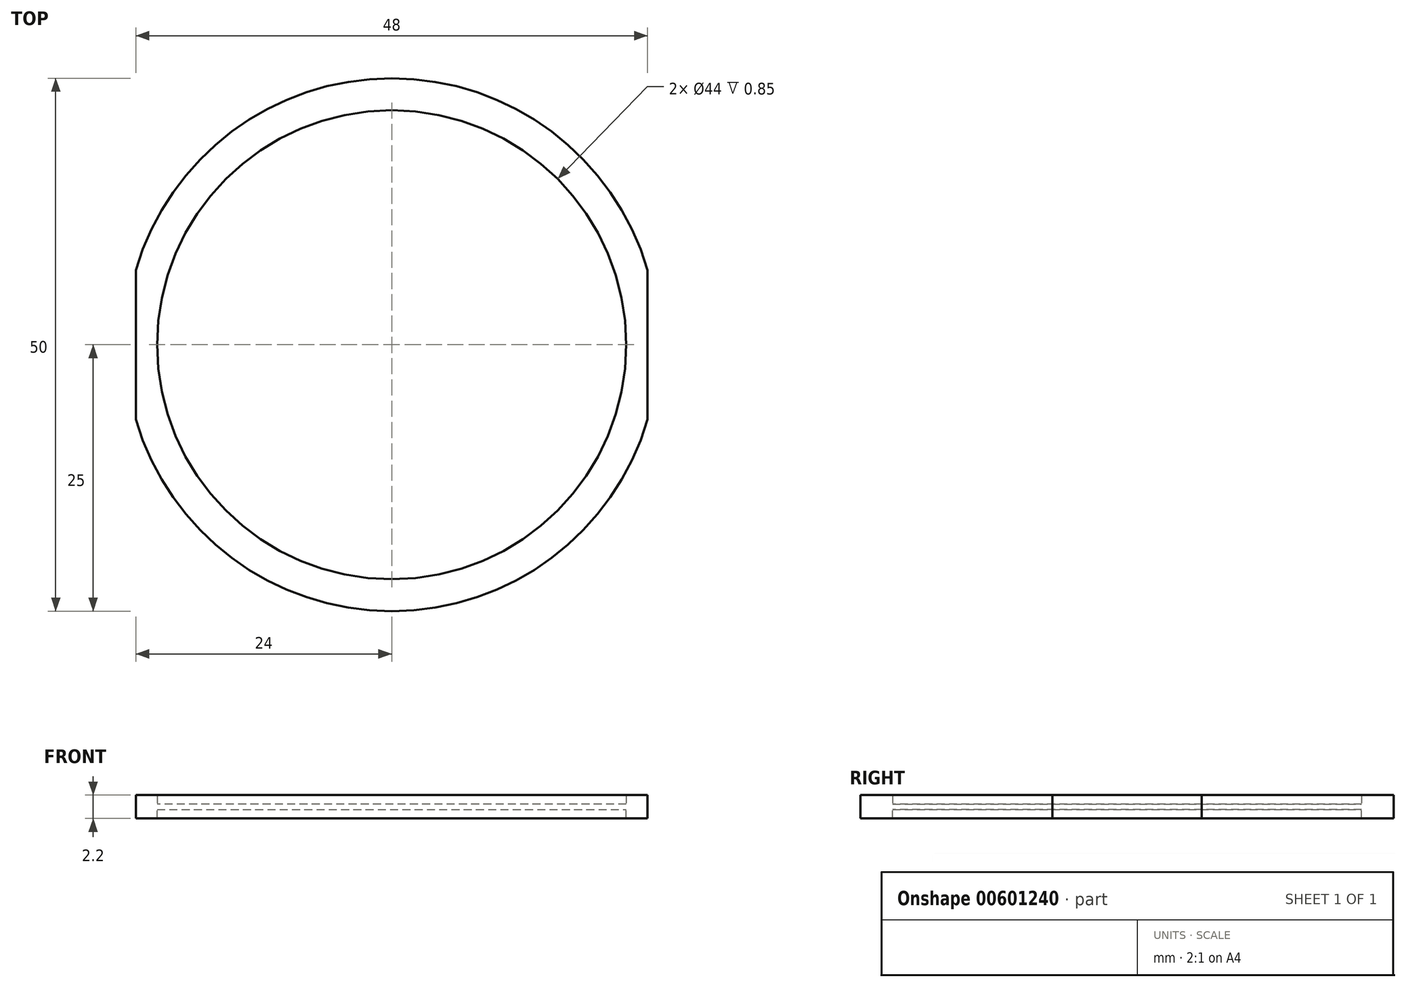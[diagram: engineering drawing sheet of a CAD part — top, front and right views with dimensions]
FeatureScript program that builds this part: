
annotation { "Feature Type Name" : "Feature", "Feature Type Description" : "" }
export const myFeature = defineFeature(function(context is Context, id is Id, definition is map)
    precondition{}
    {
        {
            var Q0;
            Q0=qCreatedBy(makeId("Top.planeOp"),FACE);
            var sketch = newSketch(context, id + "F0", { "sketchPlane" : qUnion([Q0])});
            skArc(sketch, "E0", {"start": v(24, 7) * mm, "mid": v(0, 25) * mm, "end": v(-24, 7) * mm});
            skLineSegment(sketch, "E1.left", {"start": v(-24, 7) * mm, "end": v(-24, -7) * mm});
            skLineSegment(sketch, "E1.right", {"start": v(24, 7) * mm, "end": v(24, -7) * mm});
            skArc(sketch, "E2.trimOffspring", {"start": v(-24, -7) * mm, "mid": v(0, -25) * mm, "end": v(24, -7) * mm});
            skSolve(sketch);
        }
        {
            var Q0;
            Q0=makeQuery(id+"F0.imprint","IMPRINT",FACE,{"disambiguationData":[TD([[makeQuery(id+"F0.imprint","IMPRINT",EDGE,{"derivedFrom":sQuery(id+"F0.wireOp",EDGE,"E0")}),1.0]])]});
            extrude(context, id + "F1", {"entities" : qUnion([Q0]), "depth" : 0.5 * mm, "offsetDistance" : 25 * mm});
        }
        {
            var Q0;
            Q0=makeQuery(id+"F1.opExtrude","CAP_FACE",FACE,{"disambiguationData":[OSD([sQuery(id+"F0.wireOp",EDGE,"E0"),sQuery(id+"F0.wireOp",EDGE,"E1.left"),sQuery(id+"F0.wireOp",EDGE,"E1.right"),sQuery(id+"F0.wireOp",EDGE,"E2.trimOffspring")])],"isStart":false});
            var sketch = newSketch(context, id + "F2", { "sketchPlane" : qUnion([Q0])});
            skCircle(sketch, "E3", {"center": v(0, 0) * mm, "radius": 22 * mm});
            skArc(sketch, "E4", {"start": v(24, -7) * mm, "mid": v(0, -25) * mm, "end": v(-24, -7) * mm});
            skArc(sketch, "E5", {"start": v(-24, 7) * mm, "mid": v(0, 25) * mm, "end": v(24, 7) * mm});
            skLineSegment(sketch, "E6", {"start": v(24, 7) * mm, "end": v(24, -7) * mm});
            skLineSegment(sketch, "E7", {"start": v(-24, 7) * mm, "end": v(-24, -7) * mm});
            skSolve(sketch);
        }
        {
            var Q0;
            Q0=makeQuery(id+"F2.imprint","IMPRINT",FACE,{"disambiguationData":[TD([[makeQuery(id+"F2.imprint","IMPRINT",EDGE,{"derivedFrom":sQuery(id+"F2.wireOp",EDGE,"E3")}),-1.0]])]});
            extrude(context, id + "F3", {"entities" : qUnion([Q0]), "operationType" : NewBodyOperationType.ADD, "depth" : 0.85 * mm, "offsetDistance" : 25 * mm});
        }
        {
            var Q0;
            Q0=makeQuery(id+"F1.opExtrude","CAP_FACE",FACE,{"disambiguationData":[OSD([sQuery(id+"F0.wireOp",EDGE,"E0"),sQuery(id+"F0.wireOp",EDGE,"E1.left"),sQuery(id+"F0.wireOp",EDGE,"E1.right"),sQuery(id+"F0.wireOp",EDGE,"E2.trimOffspring")])],"isStart":true});
            var sketch = newSketch(context, id + "F4", { "sketchPlane" : qUnion([Q0])});
            skCircle(sketch, "E8", {"center": v(0, 0) * mm, "radius": 22 * mm});
            skArc(sketch, "E9", {"start": v(-24, 7) * mm, "mid": v(0, 25) * mm, "end": v(24, 7) * mm});
            skArc(sketch, "E10", {"start": v(24, -7) * mm, "mid": v(0, -25) * mm, "end": v(-24, -7) * mm});
            skLineSegment(sketch, "E11", {"start": v(24, 7) * mm, "end": v(24, -7) * mm});
            skLineSegment(sketch, "E12", {"start": v(-24, 7) * mm, "end": v(-24, -7) * mm});
            skSolve(sketch);
        }
        {
            var Q0;
            Q0=makeQuery(id+"F4.imprint","IMPRINT",FACE,{"disambiguationData":[TD([[makeQuery(id+"F4.imprint","IMPRINT",EDGE,{"derivedFrom":sQuery(id+"F4.wireOp",EDGE,"E8")}),-1.0]])]});
            extrude(context, id + "F5", {"entities" : qUnion([Q0]), "operationType" : NewBodyOperationType.ADD, "depth" : 0.85 * mm, "offsetDistance" : 25 * mm});
        }
    });
